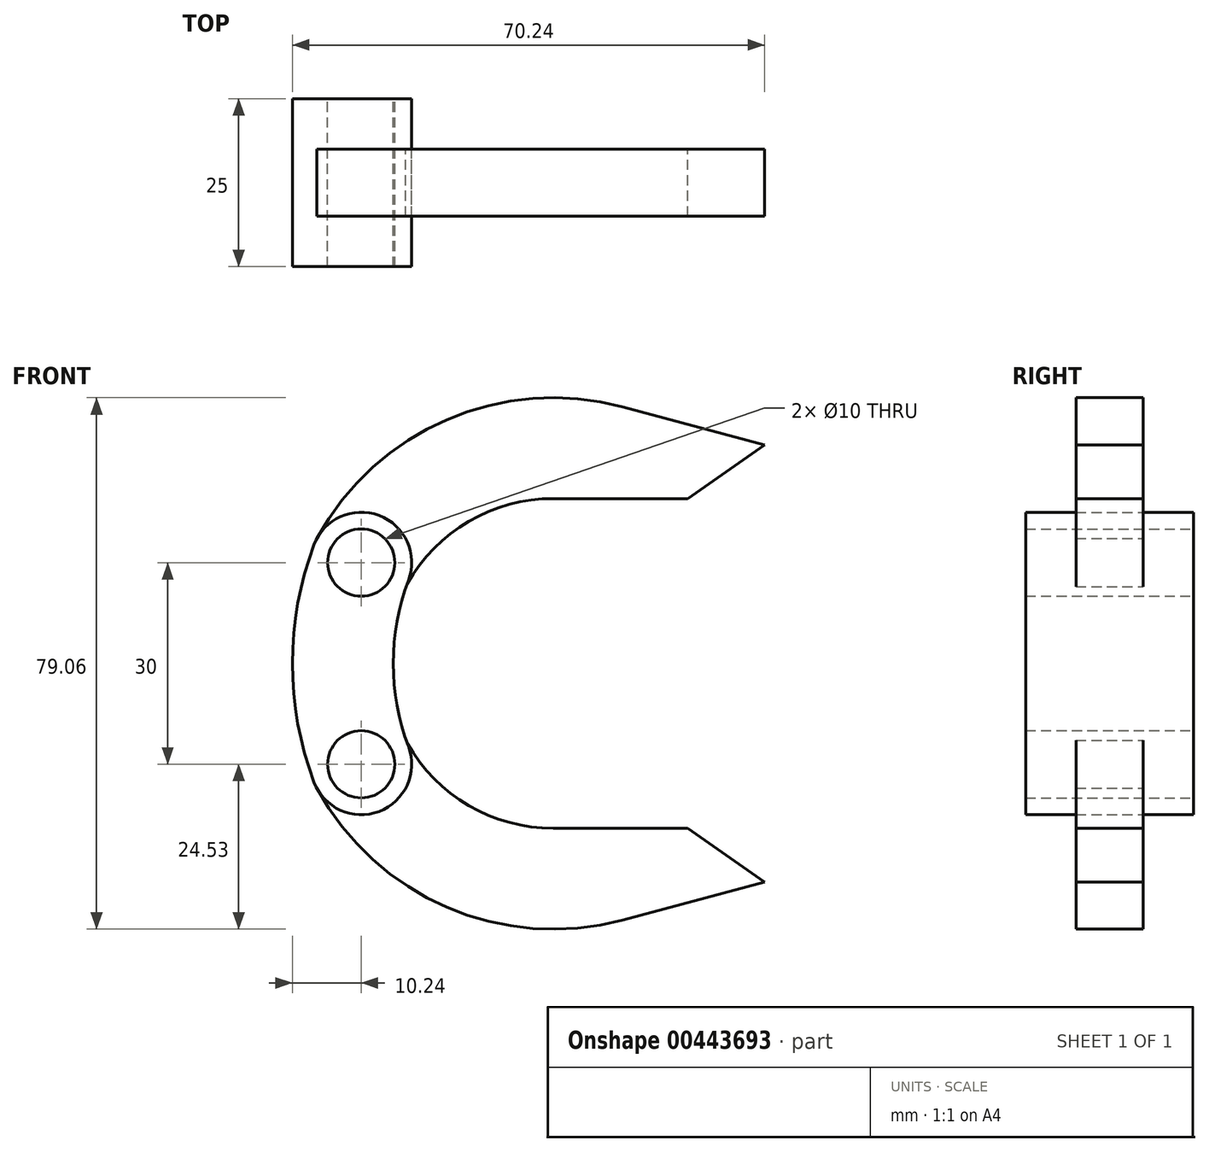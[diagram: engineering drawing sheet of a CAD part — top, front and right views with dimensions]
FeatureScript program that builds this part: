
annotation { "Feature Type Name" : "Feature", "Feature Type Description" : "" }
export const myFeature = defineFeature(function(context is Context, id is Id, definition is map)
    precondition{}
    {
        {
            var Q0;
            Q0=qCreatedBy(makeId("Front.planeOp"),FACE);
            var sketch = newSketch(context, id + "F0", { "sketchPlane" : qUnion([Q0])});
            skLineSegment(sketch, "E0", {"start": v(0, 15) * mm, "end": v(0, -15) * mm, "construction": true});
            skLineSegment(sketch, "E1", {"start": v(0, 0) * mm, "end": v(80, 0) * mm, "construction": true});
            skCircle(sketch, "E2", {"center": v(0, 15) * mm, "radius": 5 * mm});
            skCircle(sketch, "E3", {"center": v(0, -15) * mm, "radius": 5 * mm});
            skArc(sketch, "E4.0", {"start": v(7.02, 12.35) * mm, "mid": v(2.65, 22.02) * mm, "end": v(-7.02, 17.65) * mm});
            skArc(sketch, "E5", {"start": v(-7.02, 17.65) * mm, "mid": v(-10.24, 0) * mm, "end": v(-7.02, -17.65) * mm});
            skArc(sketch, "E6", {"start": v(7.02, -12.35) * mm, "mid": v(4.76, 0) * mm, "end": v(7.02, 12.35) * mm});
            skArc(sketch, "E7.0", {"start": v(-7.02, -17.65) * mm, "mid": v(2.65, -22.02) * mm, "end": v(7.02, -12.35) * mm});
            skSolve(sketch);
        }
        {
            var Q0;
            Q0=qCreatedBy(makeId("Front.planeOp"),FACE);
            var sketch = newSketch(context, id + "F1", { "sketchPlane" : qUnion([Q0])});
            skCircle(sketch, "E8.0", {"center": v(0, 15) * mm, "radius": 5 * mm});
            skCircle(sketch, "E9", {"center": v(0, 15) * mm, "radius": 7.5 * mm});
            skCircle(sketch, "E10", {"center": v(0, -15) * mm, "radius": 7.5 * mm});
            skLineSegment(sketch, "E11", {"start": v(38.92, 38.17) * mm, "end": v(60, 32.53) * mm});
            skLineSegment(sketch, "E12", {"start": v(60, 32.53) * mm, "end": v(48.58, 24.53) * mm});
            skLineSegment(sketch, "E13", {"start": v(48.58, 24.53) * mm, "end": v(28.58, 24.53) * mm});
            skArc(sketch, "E14", {"start": v(38.92, 38.17) * mm, "mid": v(12.76, 36.27) * mm, "end": v(-6.6, 18.57) * mm});
            skArc(sketch, "E15", {"start": v(28.58, 24.53) * mm, "mid": v(15.79, 21) * mm, "end": v(6.6, 11.43) * mm});
            skPoint(sketch, "E16.orphan", {"position": v(3.59, 0) * mm});
            skLineSegment(sketch, "E17", {"start": v(38.92, 38.17) * mm, "end": v(37.45, 29.8) * mm, "construction": true});
            skLineSegment(sketch, "E18", {"start": v(37.1, 27.83) * mm, "end": v(22.61, 31.7) * mm, "construction": true});
            skArc(sketch, "E19", {"start": v(23.13, 33.64) * mm, "mid": v(20.68, 32.23) * mm, "end": v(22.1, 29.78) * mm});
            skArc(sketch, "E20", {"start": v(36.59, 25.9) * mm, "mid": v(39.06, 27.4) * mm, "end": v(37.45, 29.8) * mm});
            skLineSegment(sketch, "E21", {"start": v(23.13, 33.64) * mm, "end": v(37.45, 29.8) * mm});
            skLineSegment(sketch, "E22", {"start": v(22.1, 29.78) * mm, "end": v(36.59, 25.9) * mm});
            skArc(sketch, "E23.MirrorCS", {"start": v(23.13, -33.64) * mm, "mid": v(20.68, -32.23) * mm, "end": v(22.1, -29.78) * mm});
            skArc(sketch, "E24.MirrorCS", {"start": v(36.59, -25.9) * mm, "mid": v(39.06, -27.4) * mm, "end": v(37.45, -29.8) * mm});
            skLineSegment(sketch, "E25.MirrorCS", {"start": v(22.1, -29.78) * mm, "end": v(36.59, -25.9) * mm});
            skLineSegment(sketch, "E26.MirrorCS", {"start": v(23.13, -33.64) * mm, "end": v(37.45, -29.8) * mm});
            skLineSegment(sketch, "E27.MirrorCS", {"start": v(38.92, -38.17) * mm, "end": v(60, -32.53) * mm});
            skArc(sketch, "E28.MirrorCS", {"start": v(38.92, -38.17) * mm, "mid": v(12.76, -36.27) * mm, "end": v(-6.6, -18.57) * mm});
            skLineSegment(sketch, "E29.MirrorCS", {"start": v(48.58, -24.53) * mm, "end": v(28.58, -24.53) * mm});
            skLineSegment(sketch, "E30.MirrorCS", {"start": v(60, -32.53) * mm, "end": v(48.58, -24.53) * mm});
            skArc(sketch, "E31.MirrorCS", {"start": v(28.58, -24.53) * mm, "mid": v(15.79, -21) * mm, "end": v(6.6, -11.43) * mm});
            skSolve(sketch);
        }
        {
            var Q0;
            Q0=makeQuery(id+"F0.imprint","IMPRINT",FACE,{"disambiguationData":[TD([[makeQuery(id+"F0.imprint","IMPRINT",EDGE,{"derivedFrom":sQuery(id+"F0.wireOp",EDGE,"E2")}),-1.0]])]});
            extrude(context, id + "F2", {"entities" : qUnion([Q0]), "endBound" : BoundingType.SYMMETRIC, "depth" : 25 * mm});
        }
        {
            var Q0;
            Q0=makeQuery(id+"F1.imprint","IMPRINT",FACE,{"disambiguationData":[TD([[makeQuery(id+"F1.imprint","IMPRINT",EDGE,{"derivedFrom":sQuery(id+"F1.wireOp",EDGE,"E27.MirrorCS")}),1.0]])]});
            var Q1;
            Q1=makeQuery(id+"F1.imprint","IMPRINT",FACE,{"disambiguationData":[TD([[makeQuery(id+"F1.imprint","IMPRINT",EDGE,{"derivedFrom":sQuery(id+"F1.wireOp",EDGE,"E11")}),-1.0]])]});
            extrude(context, id + "F3", {"entities" : qUnion([Q0, Q1]), "endBound" : BoundingType.SYMMETRIC, "depth" : 10 * mm});
        }
    });
